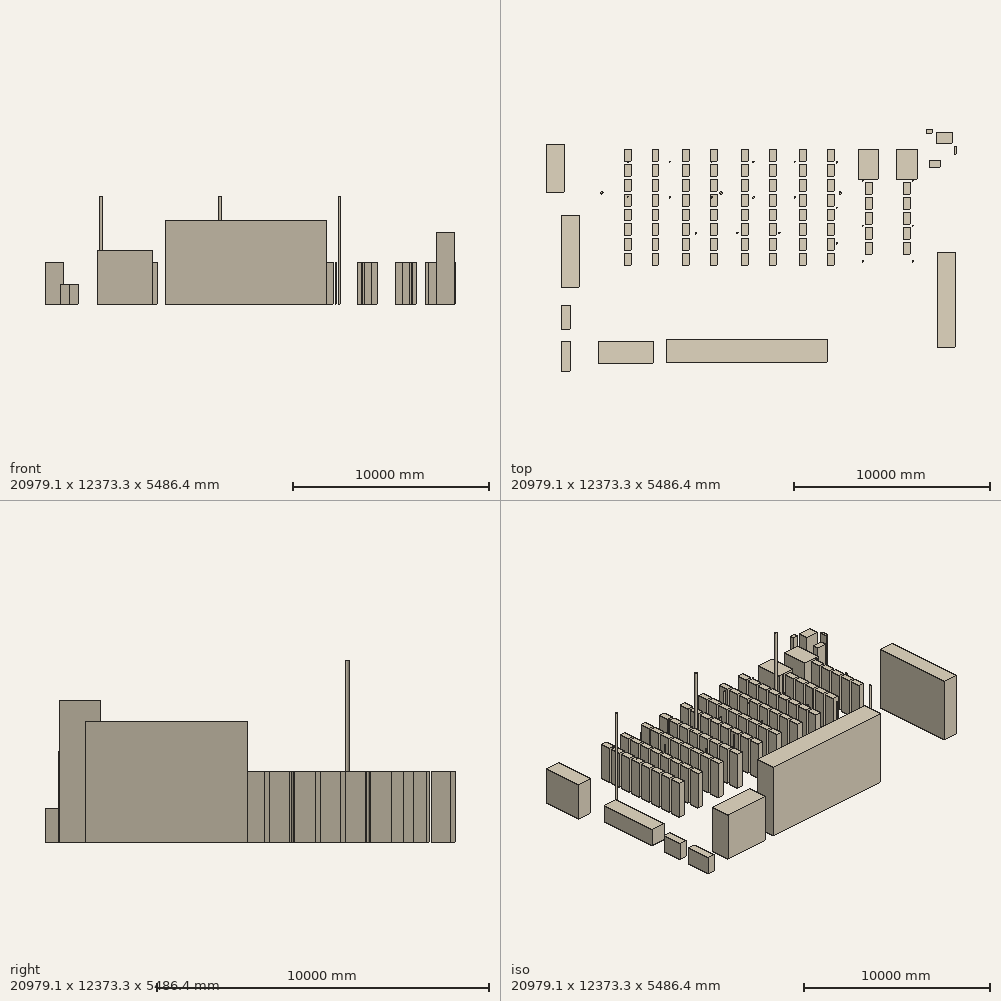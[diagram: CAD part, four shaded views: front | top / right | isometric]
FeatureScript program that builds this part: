
annotation { "Feature Type Name" : "Feature", "Feature Type Description" : "" }
export const myFeature = defineFeature(function(context is Context, id is Id, definition is map)
    precondition{}
    {
        {
            var Q0;
            Q0=qCreatedBy(makeId("Top.planeOp"),FACE);
            var sketch = newSketch(context, id + "F0", { "sketchPlane" : qUnion([Q0])});
            skLineSegment(sketch, "E0", {"start": v(-10502.58, 3251.2) * mm, "end": v(10477.82, 3251.2) * mm});
            skLineSegment(sketch, "E1", {"start": v(-10502.58, 3251.2) * mm, "end": v(-10502.58, 0) * mm});
            skLineSegment(sketch, "E2", {"start": v(-10502.58, 0) * mm, "end": v(-9740.58, 0) * mm});
            skLineSegment(sketch, "E3", {"start": v(-9740.58, 0) * mm, "end": v(-9740.58, -10033) * mm});
            skLineSegment(sketch, "E4", {"start": v(-9740.58, -10033) * mm, "end": v(-7810.18, -10033) * mm});
            skLineSegment(sketch, "E5", {"start": v(-7810.18, -10033) * mm, "end": v(-7810.18, -8839.2) * mm});
            skLineSegment(sketch, "E6", {"start": v(10477.82, 3251.2) * mm, "end": v(10477.82, -8051.8) * mm});
            skLineSegment(sketch, "E7", {"start": v(10477.82, -8051.8) * mm, "end": v(6007.42, -8051.8) * mm});
            skLineSegment(sketch, "E8", {"start": v(6007.42, -8051.8) * mm, "end": v(6007.42, -8839.2) * mm});
            skLineSegment(sketch, "E9", {"start": v(6007.42, -8839.2) * mm, "end": v(-7810.18, -8839.2) * mm});
            skSolve(sketch);
        }
        {
            var Q0;
            Q0=makeQuery(id+"F0.imprint","IMPRINT",FACE,{"disambiguationData":[TD([[makeQuery(id+"F0.imprint","IMPRINT",EDGE,{"derivedFrom":sQuery(id+"F0.wireOp",EDGE,"E0")}),-1.0]])]});
            var sketch = newSketch(context, id + "F1", { "sketchPlane" : qUnion([Q0])});
            skCircle(sketch, "E10", {"center": v(-7657.78, 0) * mm, "radius": 63.5 * mm});
            skCircle(sketch, "E11", {"center": v(-1561.78, 0) * mm, "radius": 63.5 * mm});
            skCircle(sketch, "E12", {"center": v(4534.22, 0) * mm, "radius": 63.5 * mm});
            skSolve(sketch);
        }
        {
            var Q0;
            Q0=makeQuery(id+"F0.imprint","IMPRINT",FACE,{"disambiguationData":[TD([[makeQuery(id+"F0.imprint","IMPRINT",EDGE,{"derivedFrom":sQuery(id+"F0.wireOp",EDGE,"E0")}),-1.0]])]});
            var sketch = newSketch(context, id + "F2", { "sketchPlane" : qUnion([Q0])});
            skLineSegment(sketch, "E13.bottom", {"start": v(9436.42, 3098.8) * mm, "end": v(10249.22, 3098.8) * mm});
            skLineSegment(sketch, "E13.top", {"start": v(9436.42, 2540) * mm, "end": v(10249.22, 2540) * mm});
            skLineSegment(sketch, "E13.left", {"start": v(9436.42, 3098.8) * mm, "end": v(9436.42, 2540) * mm});
            skLineSegment(sketch, "E13.right", {"start": v(10249.22, 3098.8) * mm, "end": v(10249.22, 2540) * mm});
            skLineSegment(sketch, "E14.bottom", {"start": v(9072.21, 1676.4) * mm, "end": v(9681.81, 1676.4) * mm});
            skLineSegment(sketch, "E14.top", {"start": v(9072.21, 1320.8) * mm, "end": v(9681.81, 1320.8) * mm});
            skLineSegment(sketch, "E14.left", {"start": v(9072.21, 1676.4) * mm, "end": v(9072.21, 1320.8) * mm});
            skLineSegment(sketch, "E14.right", {"start": v(9681.81, 1676.4) * mm, "end": v(9681.81, 1320.8) * mm});
            skLineSegment(sketch, "E15.bottom", {"start": v(8928.42, 3251.2) * mm, "end": v(9233.22, 3251.2) * mm});
            skLineSegment(sketch, "E15.top", {"start": v(8928.42, 3048) * mm, "end": v(9233.22, 3048) * mm});
            skLineSegment(sketch, "E15.left", {"start": v(8928.42, 3251.2) * mm, "end": v(8928.42, 3048) * mm});
            skLineSegment(sketch, "E15.right", {"start": v(9233.22, 3251.2) * mm, "end": v(9233.22, 3048) * mm});
            skLineSegment(sketch, "E16.bottom", {"start": v(10477.82, 2387.6) * mm, "end": v(10350.82, 2387.6) * mm});
            skLineSegment(sketch, "E16.top", {"start": v(10477.82, 1981.2) * mm, "end": v(10350.82, 1981.2) * mm});
            skLineSegment(sketch, "E16.left", {"start": v(10477.82, 2387.6) * mm, "end": v(10477.82, 1981.2) * mm});
            skLineSegment(sketch, "E16.right", {"start": v(10350.82, 2387.6) * mm, "end": v(10350.82, 1981.2) * mm});
            skSolve(sketch);
        }
        {
            var Q0;
            Q0=makeQuery(id+"F0.imprint","IMPRINT",FACE,{"disambiguationData":[TD([[makeQuery(id+"F0.imprint","IMPRINT",EDGE,{"derivedFrom":sQuery(id+"F0.wireOp",EDGE,"E0")}),-1.0]])]});
            var sketch = newSketch(context, id + "F3", { "sketchPlane" : qUnion([Q0])});
            skLineSegment(sketch, "E17.bottom", {"start": v(-9740.58, -1168.4) * mm, "end": v(-8826.18, -1168.4) * mm});
            skLineSegment(sketch, "E17.top", {"start": v(-9740.58, -2997.2) * mm, "end": v(-8826.18, -2997.2) * mm});
            skLineSegment(sketch, "E17.left", {"start": v(-9740.58, -1168.4) * mm, "end": v(-9740.58, -2997.2) * mm});
            skLineSegment(sketch, "E17.right", {"start": v(-8826.18, -1168.4) * mm, "end": v(-8826.18, -2997.2) * mm});
            skLineSegment(sketch, "E18.bottom", {"start": v(-9740.58, -9122.12) * mm, "end": v(-9283.38, -9122.12) * mm});
            skLineSegment(sketch, "E18.top", {"start": v(-9740.58, -7598.12) * mm, "end": v(-9283.38, -7598.12) * mm});
            skLineSegment(sketch, "E18.left", {"start": v(-9740.58, -9122.12) * mm, "end": v(-9740.58, -7598.12) * mm});
            skLineSegment(sketch, "E18.right", {"start": v(-9283.38, -9122.12) * mm, "end": v(-9283.38, -7598.12) * mm});
            skLineSegment(sketch, "E19.top", {"start": v(-9740.58, -4826) * mm, "end": v(-8826.18, -4826) * mm});
            skLineSegment(sketch, "E19.left", {"start": v(-9740.58, -2997.2) * mm, "end": v(-9740.58, -4826) * mm});
            skLineSegment(sketch, "E19.right", {"start": v(-8826.18, -2997.2) * mm, "end": v(-8826.18, -4826) * mm});
            skLineSegment(sketch, "E20.bottom", {"start": v(-9740.58, -5740.4) * mm, "end": v(-9283.38, -5740.4) * mm});
            skLineSegment(sketch, "E20.top", {"start": v(-9740.58, -6959.6) * mm, "end": v(-9283.38, -6959.6) * mm});
            skLineSegment(sketch, "E20.left", {"start": v(-9740.58, -5740.4) * mm, "end": v(-9740.58, -6959.6) * mm});
            skLineSegment(sketch, "E20.right", {"start": v(-9283.38, -5740.4) * mm, "end": v(-9283.38, -6959.6) * mm});
            skSolve(sketch);
        }
        {
            var Q0;
            Q0=makeQuery(id+"F0.imprint","IMPRINT",FACE,{"disambiguationData":[TD([[makeQuery(id+"F0.imprint","IMPRINT",EDGE,{"derivedFrom":sQuery(id+"F0.wireOp",EDGE,"E0")}),-1.0]])]});
            var sketch = newSketch(context, id + "F4", { "sketchPlane" : qUnion([Q0])});
            skLineSegment(sketch, "E21.bottom", {"start": v(-7846.94, -8737.6) * mm, "end": v(-6424.54, -8737.6) * mm});
            skLineSegment(sketch, "E21.top", {"start": v(-7846.94, -7569.2) * mm, "end": v(-6424.54, -7569.2) * mm});
            skLineSegment(sketch, "E21.left", {"start": v(-7846.94, -8737.6) * mm, "end": v(-7846.94, -7569.2) * mm});
            skLineSegment(sketch, "E21.right", {"start": v(-6424.54, -8737.6) * mm, "end": v(-6424.54, -7569.2) * mm});
            skLineSegment(sketch, "E22.bottom", {"start": v(-6424.54, -8737.6) * mm, "end": v(-5002.14, -8737.6) * mm});
            skLineSegment(sketch, "E22.top", {"start": v(-6424.54, -7569.2) * mm, "end": v(-5002.14, -7569.2) * mm});
            skLineSegment(sketch, "E22.right", {"start": v(-5002.14, -8737.6) * mm, "end": v(-5002.14, -7569.2) * mm});
            skSolve(sketch);
        }
        {
            var Q0;
            Q0=makeQuery(id+"F0.imprint","IMPRINT",FACE,{"disambiguationData":[TD([[makeQuery(id+"F0.imprint","IMPRINT",EDGE,{"derivedFrom":sQuery(id+"F0.wireOp",EDGE,"E0")}),-1.0]])]});
            var sketch = newSketch(context, id + "F5", { "sketchPlane" : qUnion([Q0])});
            skLineSegment(sketch, "E23.bottom", {"start": v(-4355.78, -8686.8) * mm, "end": v(3873.82, -8686.8) * mm});
            skLineSegment(sketch, "E23.top", {"start": v(-4355.78, -7467.6) * mm, "end": v(3873.82, -7467.6) * mm});
            skLineSegment(sketch, "E23.left", {"start": v(-4355.78, -8686.8) * mm, "end": v(-4355.78, -7467.6) * mm});
            skLineSegment(sketch, "E23.right", {"start": v(3873.82, -8686.8) * mm, "end": v(3873.82, -7467.6) * mm});
            skSolve(sketch);
        }
        {
            var Q0;
            Q0=makeQuery(id+"F0.imprint","IMPRINT",FACE,{"disambiguationData":[TD([[makeQuery(id+"F0.imprint","IMPRINT",EDGE,{"derivedFrom":sQuery(id+"F0.wireOp",EDGE,"E0")}),-1.0]])]});
            var sketch = newSketch(context, id + "F6", { "sketchPlane" : qUnion([Q0])});
            skLineSegment(sketch, "E24.bottom", {"start": v(10427.02, -3022.6) * mm, "end": v(9512.62, -3022.6) * mm});
            skLineSegment(sketch, "E24.top", {"start": v(10427.02, -7899.4) * mm, "end": v(9512.62, -7899.4) * mm});
            skLineSegment(sketch, "E24.left", {"start": v(10427.02, -3022.6) * mm, "end": v(10427.02, -7899.4) * mm});
            skLineSegment(sketch, "E24.right", {"start": v(9512.62, -3022.6) * mm, "end": v(9512.62, -7899.4) * mm});
            skSolve(sketch);
        }
        {
            var Q0;
            Q0=makeQuery(id+"F0.imprint","IMPRINT",FACE,{"disambiguationData":[TD([[makeQuery(id+"F0.imprint","IMPRINT",EDGE,{"derivedFrom":sQuery(id+"F0.wireOp",EDGE,"E0")}),-1.0]])]});
            var sketch = newSketch(context, id + "F7", { "sketchPlane" : qUnion([Q0])});
            skLineSegment(sketch, "E25.bottom", {"start": v(8462.61, 1719.58) * mm, "end": v(7421.21, 1719.58) * mm});
            skLineSegment(sketch, "E25.top", {"start": v(8462.61, 2235.2) * mm, "end": v(7421.21, 2235.2) * mm});
            skLineSegment(sketch, "E25.left", {"start": v(8462.61, 1719.58) * mm, "end": v(8462.61, 2235.2) * mm});
            skLineSegment(sketch, "E25.right", {"start": v(7421.21, 1719.58) * mm, "end": v(7421.21, 2235.2) * mm});
            skPoint(sketch, "E25.middle", {"position": v(7941.91, 1977.4) * mm});
            skLineSegment(sketch, "E26.bottom", {"start": v(6506.81, 1719.58) * mm, "end": v(5465.41, 1719.58) * mm});
            skLineSegment(sketch, "E26.top", {"start": v(6506.81, 2235.2) * mm, "end": v(5465.41, 2235.2) * mm});
            skLineSegment(sketch, "E26.left", {"start": v(6506.81, 1719.58) * mm, "end": v(6506.81, 2235.2) * mm});
            skLineSegment(sketch, "E26.right", {"start": v(5465.41, 1719.58) * mm, "end": v(5465.41, 2235.2) * mm});
            skPoint(sketch, "E26.middle", {"position": v(5986.11, 1977.4) * mm});
            skLineSegment(sketch, "E27.bottom", {"start": v(8462.61, 1203.96) * mm, "end": v(7421.21, 1203.96) * mm});
            skLineSegment(sketch, "E27.left", {"start": v(8462.61, 1203.96) * mm, "end": v(8462.61, 1719.58) * mm});
            skLineSegment(sketch, "E27.right", {"start": v(7421.21, 1203.96) * mm, "end": v(7421.21, 1719.58) * mm});
            skPoint(sketch, "E27.middle", {"position": v(7941.91, 1461.77) * mm});
            skLineSegment(sketch, "E28.bottom", {"start": v(6506.81, 1203.96) * mm, "end": v(5465.41, 1203.96) * mm});
            skLineSegment(sketch, "E28.left", {"start": v(6506.81, 1203.96) * mm, "end": v(6506.81, 1719.58) * mm});
            skLineSegment(sketch, "E28.right", {"start": v(5465.41, 1203.96) * mm, "end": v(5465.41, 1719.58) * mm});
            skPoint(sketch, "E28.middle", {"position": v(5986.11, 1461.77) * mm});
            skLineSegment(sketch, "E29.bottom", {"start": v(6506.81, 688.34) * mm, "end": v(5465.41, 688.34) * mm});
            skLineSegment(sketch, "E29.left", {"start": v(6506.81, 688.34) * mm, "end": v(6506.81, 1203.96) * mm});
            skLineSegment(sketch, "E29.right", {"start": v(5465.41, 688.34) * mm, "end": v(5465.41, 1203.96) * mm});
            skPoint(sketch, "E29.middle", {"position": v(5986.11, 946.15) * mm});
            skLineSegment(sketch, "E30.bottom", {"start": v(8462.61, 688.34) * mm, "end": v(7421.21, 688.34) * mm});
            skLineSegment(sketch, "E30.left", {"start": v(8462.61, 688.34) * mm, "end": v(8462.61, 1203.96) * mm});
            skLineSegment(sketch, "E30.right", {"start": v(7421.21, 688.34) * mm, "end": v(7421.21, 1203.96) * mm});
            skPoint(sketch, "E30.middle", {"position": v(7941.91, 946.15) * mm});
            skLineSegment(sketch, "E31.bottom", {"start": v(6163.91, -73.66) * mm, "end": v(5808.31, -73.66) * mm});
            skLineSegment(sketch, "E31.top", {"start": v(6163.91, 535.94) * mm, "end": v(5808.31, 535.94) * mm});
            skLineSegment(sketch, "E31.left", {"start": v(6163.91, -73.66) * mm, "end": v(6163.91, 535.94) * mm});
            skLineSegment(sketch, "E31.right", {"start": v(5808.31, -73.66) * mm, "end": v(5808.31, 535.94) * mm});
            skPoint(sketch, "E31.middle", {"position": v(5986.11, 231.14) * mm});
            skLineSegment(sketch, "E32.bottom", {"start": v(6163.91, -835.66) * mm, "end": v(5808.31, -835.66) * mm});
            skLineSegment(sketch, "E32.top", {"start": v(6163.91, -226.06) * mm, "end": v(5808.31, -226.06) * mm});
            skLineSegment(sketch, "E32.left", {"start": v(6163.91, -835.66) * mm, "end": v(6163.91, -226.06) * mm});
            skLineSegment(sketch, "E32.right", {"start": v(5808.31, -835.66) * mm, "end": v(5808.31, -226.06) * mm});
            skPoint(sketch, "E32.middle", {"position": v(5986.11, -530.86) * mm});
            skLineSegment(sketch, "E33.bottom", {"start": v(6163.91, -1597.66) * mm, "end": v(5808.31, -1597.66) * mm});
            skLineSegment(sketch, "E33.top", {"start": v(6163.91, -988.06) * mm, "end": v(5808.31, -988.06) * mm});
            skLineSegment(sketch, "E33.left", {"start": v(6163.91, -1597.66) * mm, "end": v(6163.91, -988.06) * mm});
            skLineSegment(sketch, "E33.right", {"start": v(5808.31, -1597.66) * mm, "end": v(5808.31, -988.06) * mm});
            skPoint(sketch, "E33.middle", {"position": v(5986.11, -1292.86) * mm});
            skLineSegment(sketch, "E34.bottom", {"start": v(7764.11, -73.66) * mm, "end": v(8119.71, -73.66) * mm});
            skLineSegment(sketch, "E34.top", {"start": v(7764.11, 535.94) * mm, "end": v(8119.71, 535.94) * mm});
            skLineSegment(sketch, "E34.left", {"start": v(7764.11, -73.66) * mm, "end": v(7764.11, 535.94) * mm});
            skLineSegment(sketch, "E34.right", {"start": v(8119.71, -73.66) * mm, "end": v(8119.71, 535.94) * mm});
            skPoint(sketch, "E34.middle", {"position": v(7941.91, 231.14) * mm});
            skLineSegment(sketch, "E35.bottom", {"start": v(7764.11, -835.66) * mm, "end": v(8119.71, -835.66) * mm});
            skLineSegment(sketch, "E35.top", {"start": v(7764.11, -226.06) * mm, "end": v(8119.71, -226.06) * mm});
            skLineSegment(sketch, "E35.left", {"start": v(7764.11, -835.66) * mm, "end": v(7764.11, -226.06) * mm});
            skLineSegment(sketch, "E35.right", {"start": v(8119.71, -835.66) * mm, "end": v(8119.71, -226.06) * mm});
            skPoint(sketch, "E35.middle", {"position": v(7941.91, -530.86) * mm});
            skLineSegment(sketch, "E36.bottom", {"start": v(7764.11, -1597.66) * mm, "end": v(8119.71, -1597.66) * mm});
            skLineSegment(sketch, "E36.top", {"start": v(7764.11, -988.06) * mm, "end": v(8119.71, -988.06) * mm});
            skLineSegment(sketch, "E36.left", {"start": v(7764.11, -1597.66) * mm, "end": v(7764.11, -988.06) * mm});
            skLineSegment(sketch, "E36.right", {"start": v(8119.71, -1597.66) * mm, "end": v(8119.71, -988.06) * mm});
            skPoint(sketch, "E36.middle", {"position": v(7941.91, -1292.86) * mm});
            skLineSegment(sketch, "E37.bottom", {"start": v(5808.31, -1750.06) * mm, "end": v(6163.91, -1750.06) * mm});
            skLineSegment(sketch, "E37.top", {"start": v(5808.31, -2359.66) * mm, "end": v(6163.91, -2359.66) * mm});
            skLineSegment(sketch, "E37.left", {"start": v(5808.31, -1750.06) * mm, "end": v(5808.31, -2359.66) * mm});
            skLineSegment(sketch, "E37.right", {"start": v(6163.91, -1750.06) * mm, "end": v(6163.91, -2359.66) * mm});
            skPoint(sketch, "E37.middle", {"position": v(5986.11, -2054.86) * mm});
            skLineSegment(sketch, "E38.bottom", {"start": v(7764.11, -1750.06) * mm, "end": v(8119.71, -1750.06) * mm});
            skLineSegment(sketch, "E38.top", {"start": v(7764.11, -2359.66) * mm, "end": v(8119.71, -2359.66) * mm});
            skLineSegment(sketch, "E38.left", {"start": v(7764.11, -1750.06) * mm, "end": v(7764.11, -2359.66) * mm});
            skLineSegment(sketch, "E38.right", {"start": v(8119.71, -1750.06) * mm, "end": v(8119.71, -2359.66) * mm});
            skPoint(sketch, "E38.middle", {"position": v(7941.91, -2054.86) * mm});
            skLineSegment(sketch, "E39.bottom", {"start": v(5808.31, -2512.06) * mm, "end": v(6163.91, -2512.06) * mm});
            skLineSegment(sketch, "E39.top", {"start": v(5808.31, -3121.66) * mm, "end": v(6163.91, -3121.66) * mm});
            skLineSegment(sketch, "E39.left", {"start": v(5808.31, -2512.06) * mm, "end": v(5808.31, -3121.66) * mm});
            skLineSegment(sketch, "E39.right", {"start": v(6163.91, -2512.06) * mm, "end": v(6163.91, -3121.66) * mm});
            skPoint(sketch, "E39.middle", {"position": v(5986.11, -2816.86) * mm});
            skLineSegment(sketch, "E40.bottom", {"start": v(7764.11, -2512.06) * mm, "end": v(8119.71, -2512.06) * mm});
            skLineSegment(sketch, "E40.top", {"start": v(7764.11, -3121.66) * mm, "end": v(8119.71, -3121.66) * mm});
            skLineSegment(sketch, "E40.left", {"start": v(7764.11, -2512.06) * mm, "end": v(7764.11, -3121.66) * mm});
            skLineSegment(sketch, "E40.right", {"start": v(8119.71, -2512.06) * mm, "end": v(8119.71, -3121.66) * mm});
            skPoint(sketch, "E40.middle", {"position": v(7941.91, -2816.86) * mm});
            skSolve(sketch);
        }
        {
            var Q0;
            Q0=makeQuery(id+"F0.imprint","IMPRINT",FACE,{"disambiguationData":[TD([[makeQuery(id+"F0.imprint","IMPRINT",EDGE,{"derivedFrom":sQuery(id+"F0.wireOp",EDGE,"E0")}),-1.0]])]});
            var sketch = newSketch(context, id + "F8", { "sketchPlane" : qUnion([Q0])});
            skLineSegment(sketch, "E41.bottom", {"start": v(3890.61, 2235.2) * mm, "end": v(4246.21, 2235.2) * mm});
            skLineSegment(sketch, "E41.top", {"start": v(3890.61, 1625.6) * mm, "end": v(4246.21, 1625.6) * mm});
            skLineSegment(sketch, "E41.left", {"start": v(3890.61, 2235.2) * mm, "end": v(3890.61, 1625.6) * mm});
            skLineSegment(sketch, "E41.right", {"start": v(4246.21, 2235.2) * mm, "end": v(4246.21, 1625.6) * mm});
            skPoint(sketch, "E41.middle", {"position": v(4068.41, 1930.4) * mm});
            skLineSegment(sketch, "E42.bottom", {"start": v(3890.61, 1473.2) * mm, "end": v(4246.21, 1473.2) * mm});
            skLineSegment(sketch, "E42.top", {"start": v(3890.61, 863.6) * mm, "end": v(4246.21, 863.6) * mm});
            skLineSegment(sketch, "E42.left", {"start": v(3890.61, 1473.2) * mm, "end": v(3890.61, 863.6) * mm});
            skLineSegment(sketch, "E42.right", {"start": v(4246.21, 1473.2) * mm, "end": v(4246.21, 863.6) * mm});
            skPoint(sketch, "E42.middle", {"position": v(4068.41, 1168.4) * mm});
            skLineSegment(sketch, "E43.bottom", {"start": v(2468.21, 2235.2) * mm, "end": v(2823.81, 2235.2) * mm});
            skLineSegment(sketch, "E43.top", {"start": v(2468.21, 1625.6) * mm, "end": v(2823.81, 1625.6) * mm});
            skLineSegment(sketch, "E43.left", {"start": v(2468.21, 2235.2) * mm, "end": v(2468.21, 1625.6) * mm});
            skLineSegment(sketch, "E43.right", {"start": v(2823.81, 2235.2) * mm, "end": v(2823.81, 1625.6) * mm});
            skPoint(sketch, "E43.middle", {"position": v(2646.01, 1930.4) * mm});
            skLineSegment(sketch, "E44.bottom", {"start": v(2468.21, 1473.2) * mm, "end": v(2823.81, 1473.2) * mm});
            skLineSegment(sketch, "E44.top", {"start": v(2468.21, 863.6) * mm, "end": v(2823.81, 863.6) * mm});
            skLineSegment(sketch, "E44.left", {"start": v(2468.21, 1473.2) * mm, "end": v(2468.21, 863.6) * mm});
            skLineSegment(sketch, "E44.right", {"start": v(2823.81, 1473.2) * mm, "end": v(2823.81, 863.6) * mm});
            skPoint(sketch, "E44.middle", {"position": v(2646.01, 1168.4) * mm});
            skLineSegment(sketch, "E45.bottom", {"start": v(2468.21, 711.2) * mm, "end": v(2823.81, 711.2) * mm});
            skLineSegment(sketch, "E45.top", {"start": v(2468.21, 101.6) * mm, "end": v(2823.81, 101.6) * mm});
            skLineSegment(sketch, "E45.left", {"start": v(2468.21, 711.2) * mm, "end": v(2468.21, 101.6) * mm});
            skLineSegment(sketch, "E45.right", {"start": v(2823.81, 711.2) * mm, "end": v(2823.81, 101.6) * mm});
            skPoint(sketch, "E45.middle", {"position": v(2646.01, 406.4) * mm});
            skLineSegment(sketch, "E46.bottom", {"start": v(3890.61, 711.2) * mm, "end": v(4246.21, 711.2) * mm});
            skLineSegment(sketch, "E46.top", {"start": v(3890.61, 101.6) * mm, "end": v(4246.21, 101.6) * mm});
            skLineSegment(sketch, "E46.left", {"start": v(3890.61, 711.2) * mm, "end": v(3890.61, 101.6) * mm});
            skLineSegment(sketch, "E46.right", {"start": v(4246.21, 711.2) * mm, "end": v(4246.21, 101.6) * mm});
            skPoint(sketch, "E46.middle", {"position": v(4068.41, 406.4) * mm});
            skLineSegment(sketch, "E47.bottom", {"start": v(2468.21, -50.8) * mm, "end": v(2823.81, -50.8) * mm});
            skLineSegment(sketch, "E47.top", {"start": v(2468.21, -660.4) * mm, "end": v(2823.81, -660.4) * mm});
            skLineSegment(sketch, "E47.left", {"start": v(2468.21, -50.8) * mm, "end": v(2468.21, -660.4) * mm});
            skLineSegment(sketch, "E47.right", {"start": v(2823.81, -50.8) * mm, "end": v(2823.81, -660.4) * mm});
            skPoint(sketch, "E47.middle", {"position": v(2646.01, -355.6) * mm});
            skLineSegment(sketch, "E48.bottom", {"start": v(3890.61, -50.8) * mm, "end": v(4246.21, -50.8) * mm});
            skLineSegment(sketch, "E48.top", {"start": v(3890.61, -660.4) * mm, "end": v(4246.21, -660.4) * mm});
            skLineSegment(sketch, "E48.left", {"start": v(3890.61, -50.8) * mm, "end": v(3890.61, -660.4) * mm});
            skLineSegment(sketch, "E48.right", {"start": v(4246.21, -50.8) * mm, "end": v(4246.21, -660.4) * mm});
            skPoint(sketch, "E48.middle", {"position": v(4068.41, -355.6) * mm});
            skLineSegment(sketch, "E49.bottom", {"start": v(2468.21, -812.8) * mm, "end": v(2823.81, -812.8) * mm});
            skLineSegment(sketch, "E49.top", {"start": v(2468.21, -1422.4) * mm, "end": v(2823.81, -1422.4) * mm});
            skLineSegment(sketch, "E49.left", {"start": v(2468.21, -812.8) * mm, "end": v(2468.21, -1422.4) * mm});
            skLineSegment(sketch, "E49.right", {"start": v(2823.81, -812.8) * mm, "end": v(2823.81, -1422.4) * mm});
            skPoint(sketch, "E49.middle", {"position": v(2646.01, -1117.6) * mm});
            skLineSegment(sketch, "E50.bottom", {"start": v(3890.61, -812.8) * mm, "end": v(4246.21, -812.8) * mm});
            skLineSegment(sketch, "E50.top", {"start": v(3890.61, -1422.4) * mm, "end": v(4246.21, -1422.4) * mm});
            skLineSegment(sketch, "E50.left", {"start": v(3890.61, -812.8) * mm, "end": v(3890.61, -1422.4) * mm});
            skLineSegment(sketch, "E50.right", {"start": v(4246.21, -812.8) * mm, "end": v(4246.21, -1422.4) * mm});
            skPoint(sketch, "E50.middle", {"position": v(4068.41, -1117.6) * mm});
            skLineSegment(sketch, "E51.bottom", {"start": v(2468.21, -1574.8) * mm, "end": v(2823.81, -1574.8) * mm});
            skLineSegment(sketch, "E51.top", {"start": v(2468.21, -2184.4) * mm, "end": v(2823.81, -2184.4) * mm});
            skLineSegment(sketch, "E51.left", {"start": v(2468.21, -1574.8) * mm, "end": v(2468.21, -2184.4) * mm});
            skLineSegment(sketch, "E51.right", {"start": v(2823.81, -1574.8) * mm, "end": v(2823.81, -2184.4) * mm});
            skPoint(sketch, "E51.middle", {"position": v(2646.01, -1879.6) * mm});
            skLineSegment(sketch, "E52.bottom", {"start": v(3890.61, -1574.8) * mm, "end": v(4246.21, -1574.8) * mm});
            skLineSegment(sketch, "E52.top", {"start": v(3890.61, -2184.4) * mm, "end": v(4246.21, -2184.4) * mm});
            skLineSegment(sketch, "E52.left", {"start": v(3890.61, -1574.8) * mm, "end": v(3890.61, -2184.4) * mm});
            skLineSegment(sketch, "E52.right", {"start": v(4246.21, -1574.8) * mm, "end": v(4246.21, -2184.4) * mm});
            skPoint(sketch, "E52.middle", {"position": v(4068.41, -1879.6) * mm});
            skLineSegment(sketch, "E53.bottom", {"start": v(2468.21, -2336.8) * mm, "end": v(2823.81, -2336.8) * mm});
            skLineSegment(sketch, "E53.top", {"start": v(2468.21, -2946.4) * mm, "end": v(2823.81, -2946.4) * mm});
            skLineSegment(sketch, "E53.left", {"start": v(2468.21, -2336.8) * mm, "end": v(2468.21, -2946.4) * mm});
            skLineSegment(sketch, "E53.right", {"start": v(2823.81, -2336.8) * mm, "end": v(2823.81, -2946.4) * mm});
            skPoint(sketch, "E53.middle", {"position": v(2646.01, -2641.6) * mm});
            skLineSegment(sketch, "E54.bottom", {"start": v(3890.61, -2336.8) * mm, "end": v(4246.21, -2336.8) * mm});
            skLineSegment(sketch, "E54.top", {"start": v(3890.61, -2946.4) * mm, "end": v(4246.21, -2946.4) * mm});
            skLineSegment(sketch, "E54.left", {"start": v(3890.61, -2336.8) * mm, "end": v(3890.61, -2946.4) * mm});
            skLineSegment(sketch, "E54.right", {"start": v(4246.21, -2336.8) * mm, "end": v(4246.21, -2946.4) * mm});
            skPoint(sketch, "E54.middle", {"position": v(4068.41, -2641.6) * mm});
            skLineSegment(sketch, "E55.bottom", {"start": v(2468.21, -3098.8) * mm, "end": v(2823.81, -3098.8) * mm});
            skLineSegment(sketch, "E55.top", {"start": v(2468.21, -3708.4) * mm, "end": v(2823.81, -3708.4) * mm});
            skLineSegment(sketch, "E55.left", {"start": v(2468.21, -3098.8) * mm, "end": v(2468.21, -3708.4) * mm});
            skLineSegment(sketch, "E55.right", {"start": v(2823.81, -3098.8) * mm, "end": v(2823.81, -3708.4) * mm});
            skPoint(sketch, "E55.middle", {"position": v(2646.01, -3403.6) * mm});
            skLineSegment(sketch, "E56.bottom", {"start": v(4246.21, -3098.8) * mm, "end": v(3890.61, -3098.8) * mm});
            skLineSegment(sketch, "E56.top", {"start": v(4246.21, -3708.4) * mm, "end": v(3890.61, -3708.4) * mm});
            skLineSegment(sketch, "E56.left", {"start": v(4246.21, -3098.8) * mm, "end": v(4246.21, -3708.4) * mm});
            skLineSegment(sketch, "E56.right", {"start": v(3890.61, -3098.8) * mm, "end": v(3890.61, -3708.4) * mm});
            skPoint(sketch, "E56.middle", {"position": v(4068.41, -3403.6) * mm});
            skSolve(sketch);
        }
        {
            var Q0;
            Q0=makeQuery(id+"F0.imprint","IMPRINT",FACE,{"disambiguationData":[TD([[makeQuery(id+"F0.imprint","IMPRINT",EDGE,{"derivedFrom":sQuery(id+"F0.wireOp",EDGE,"E0")}),-1.0]])]});
            var sketch = newSketch(context, id + "F9", { "sketchPlane" : qUnion([Q0])});
            skLineSegment(sketch, "E57.bottom", {"start": v(893.41, 2235.2) * mm, "end": v(1249.01, 2235.2) * mm});
            skLineSegment(sketch, "E57.top", {"start": v(893.41, 1625.6) * mm, "end": v(1249.01, 1625.6) * mm});
            skLineSegment(sketch, "E57.left", {"start": v(893.41, 2235.2) * mm, "end": v(893.41, 1625.6) * mm});
            skLineSegment(sketch, "E57.right", {"start": v(1249.01, 2235.2) * mm, "end": v(1249.01, 1625.6) * mm});
            skPoint(sketch, "E57.middle", {"position": v(1071.21, 1930.4) * mm});
            skLineSegment(sketch, "E58.bottom", {"start": v(893.41, 1473.2) * mm, "end": v(1249.01, 1473.2) * mm});
            skLineSegment(sketch, "E58.top", {"start": v(893.41, 863.6) * mm, "end": v(1249.01, 863.6) * mm});
            skLineSegment(sketch, "E58.left", {"start": v(893.41, 1473.2) * mm, "end": v(893.41, 863.6) * mm});
            skLineSegment(sketch, "E58.right", {"start": v(1249.01, 1473.2) * mm, "end": v(1249.01, 863.6) * mm});
            skPoint(sketch, "E58.middle", {"position": v(1071.21, 1168.4) * mm});
            skLineSegment(sketch, "E59.bottom", {"start": v(-528.99, 2235.2) * mm, "end": v(-173.39, 2235.2) * mm});
            skLineSegment(sketch, "E59.top", {"start": v(-528.99, 1625.6) * mm, "end": v(-173.39, 1625.6) * mm});
            skLineSegment(sketch, "E59.left", {"start": v(-528.99, 2235.2) * mm, "end": v(-528.99, 1625.6) * mm});
            skLineSegment(sketch, "E59.right", {"start": v(-173.39, 2235.2) * mm, "end": v(-173.39, 1625.6) * mm});
            skPoint(sketch, "E59.middle", {"position": v(-351.19, 1930.4) * mm});
            skLineSegment(sketch, "E60.bottom", {"start": v(-528.99, 1473.2) * mm, "end": v(-173.39, 1473.2) * mm});
            skLineSegment(sketch, "E60.top", {"start": v(-528.99, 863.6) * mm, "end": v(-173.39, 863.6) * mm});
            skLineSegment(sketch, "E60.left", {"start": v(-528.99, 1473.2) * mm, "end": v(-528.99, 863.6) * mm});
            skLineSegment(sketch, "E60.right", {"start": v(-173.39, 1473.2) * mm, "end": v(-173.39, 863.6) * mm});
            skPoint(sketch, "E60.middle", {"position": v(-351.19, 1168.4) * mm});
            skLineSegment(sketch, "E61.bottom", {"start": v(-528.99, 711.2) * mm, "end": v(-173.39, 711.2) * mm});
            skLineSegment(sketch, "E61.top", {"start": v(-528.99, 101.6) * mm, "end": v(-173.39, 101.6) * mm});
            skLineSegment(sketch, "E61.left", {"start": v(-528.99, 711.2) * mm, "end": v(-528.99, 101.6) * mm});
            skLineSegment(sketch, "E61.right", {"start": v(-173.39, 711.2) * mm, "end": v(-173.39, 101.6) * mm});
            skPoint(sketch, "E61.middle", {"position": v(-351.19, 406.4) * mm});
            skLineSegment(sketch, "E62.bottom", {"start": v(893.41, 711.2) * mm, "end": v(1249.01, 711.2) * mm});
            skLineSegment(sketch, "E62.top", {"start": v(893.41, 101.6) * mm, "end": v(1249.01, 101.6) * mm});
            skLineSegment(sketch, "E62.left", {"start": v(893.41, 711.2) * mm, "end": v(893.41, 101.6) * mm});
            skLineSegment(sketch, "E62.right", {"start": v(1249.01, 711.2) * mm, "end": v(1249.01, 101.6) * mm});
            skPoint(sketch, "E62.middle", {"position": v(1071.21, 406.4) * mm});
            skLineSegment(sketch, "E63.bottom", {"start": v(-528.99, -50.8) * mm, "end": v(-173.39, -50.8) * mm});
            skLineSegment(sketch, "E63.top", {"start": v(-528.99, -660.4) * mm, "end": v(-173.39, -660.4) * mm});
            skLineSegment(sketch, "E63.left", {"start": v(-528.99, -50.8) * mm, "end": v(-528.99, -660.4) * mm});
            skLineSegment(sketch, "E63.right", {"start": v(-173.39, -50.8) * mm, "end": v(-173.39, -660.4) * mm});
            skPoint(sketch, "E63.middle", {"position": v(-351.19, -355.6) * mm});
            skLineSegment(sketch, "E64.bottom", {"start": v(893.41, -50.8) * mm, "end": v(1249.01, -50.8) * mm});
            skLineSegment(sketch, "E64.top", {"start": v(893.41, -660.4) * mm, "end": v(1249.01, -660.4) * mm});
            skLineSegment(sketch, "E64.left", {"start": v(893.41, -50.8) * mm, "end": v(893.41, -660.4) * mm});
            skLineSegment(sketch, "E64.right", {"start": v(1249.01, -50.8) * mm, "end": v(1249.01, -660.4) * mm});
            skPoint(sketch, "E64.middle", {"position": v(1071.21, -355.6) * mm});
            skLineSegment(sketch, "E65.bottom", {"start": v(-528.99, -812.8) * mm, "end": v(-173.39, -812.8) * mm});
            skLineSegment(sketch, "E65.top", {"start": v(-528.99, -1422.4) * mm, "end": v(-173.39, -1422.4) * mm});
            skLineSegment(sketch, "E65.left", {"start": v(-528.99, -812.8) * mm, "end": v(-528.99, -1422.4) * mm});
            skLineSegment(sketch, "E65.right", {"start": v(-173.39, -812.8) * mm, "end": v(-173.39, -1422.4) * mm});
            skPoint(sketch, "E65.middle", {"position": v(-351.19, -1117.6) * mm});
            skLineSegment(sketch, "E66.bottom", {"start": v(893.41, -812.8) * mm, "end": v(1249.01, -812.8) * mm});
            skLineSegment(sketch, "E66.top", {"start": v(893.41, -1422.4) * mm, "end": v(1249.01, -1422.4) * mm});
            skLineSegment(sketch, "E66.left", {"start": v(893.41, -812.8) * mm, "end": v(893.41, -1422.4) * mm});
            skLineSegment(sketch, "E66.right", {"start": v(1249.01, -812.8) * mm, "end": v(1249.01, -1422.4) * mm});
            skPoint(sketch, "E66.middle", {"position": v(1071.21, -1117.6) * mm});
            skLineSegment(sketch, "E67.bottom", {"start": v(-528.99, -1574.8) * mm, "end": v(-173.39, -1574.8) * mm});
            skLineSegment(sketch, "E67.top", {"start": v(-528.99, -2184.4) * mm, "end": v(-173.39, -2184.4) * mm});
            skLineSegment(sketch, "E67.left", {"start": v(-528.99, -1574.8) * mm, "end": v(-528.99, -2184.4) * mm});
            skLineSegment(sketch, "E67.right", {"start": v(-173.39, -1574.8) * mm, "end": v(-173.39, -2184.4) * mm});
            skPoint(sketch, "E67.middle", {"position": v(-351.19, -1879.6) * mm});
            skLineSegment(sketch, "E68.bottom", {"start": v(893.41, -1574.8) * mm, "end": v(1249.01, -1574.8) * mm});
            skLineSegment(sketch, "E68.top", {"start": v(893.41, -2184.4) * mm, "end": v(1249.01, -2184.4) * mm});
            skLineSegment(sketch, "E68.left", {"start": v(893.41, -1574.8) * mm, "end": v(893.41, -2184.4) * mm});
            skLineSegment(sketch, "E68.right", {"start": v(1249.01, -1574.8) * mm, "end": v(1249.01, -2184.4) * mm});
            skPoint(sketch, "E68.middle", {"position": v(1071.21, -1879.6) * mm});
            skLineSegment(sketch, "E69.bottom", {"start": v(-528.99, -2336.8) * mm, "end": v(-173.39, -2336.8) * mm});
            skLineSegment(sketch, "E69.top", {"start": v(-528.99, -2946.4) * mm, "end": v(-173.39, -2946.4) * mm});
            skLineSegment(sketch, "E69.left", {"start": v(-528.99, -2336.8) * mm, "end": v(-528.99, -2946.4) * mm});
            skLineSegment(sketch, "E69.right", {"start": v(-173.39, -2336.8) * mm, "end": v(-173.39, -2946.4) * mm});
            skPoint(sketch, "E69.middle", {"position": v(-351.19, -2641.6) * mm});
            skLineSegment(sketch, "E70.bottom", {"start": v(893.41, -2336.8) * mm, "end": v(1249.01, -2336.8) * mm});
            skLineSegment(sketch, "E70.top", {"start": v(893.41, -2946.4) * mm, "end": v(1249.01, -2946.4) * mm});
            skLineSegment(sketch, "E70.left", {"start": v(893.41, -2336.8) * mm, "end": v(893.41, -2946.4) * mm});
            skLineSegment(sketch, "E70.right", {"start": v(1249.01, -2336.8) * mm, "end": v(1249.01, -2946.4) * mm});
            skPoint(sketch, "E70.middle", {"position": v(1071.21, -2641.6) * mm});
            skLineSegment(sketch, "E71.bottom", {"start": v(-528.99, -3098.8) * mm, "end": v(-173.39, -3098.8) * mm});
            skLineSegment(sketch, "E71.top", {"start": v(-528.99, -3708.4) * mm, "end": v(-173.39, -3708.4) * mm});
            skLineSegment(sketch, "E71.left", {"start": v(-528.99, -3098.8) * mm, "end": v(-528.99, -3708.4) * mm});
            skLineSegment(sketch, "E71.right", {"start": v(-173.39, -3098.8) * mm, "end": v(-173.39, -3708.4) * mm});
            skPoint(sketch, "E71.middle", {"position": v(-351.19, -3403.6) * mm});
            skLineSegment(sketch, "E72.bottom", {"start": v(1249.01, -3098.8) * mm, "end": v(893.41, -3098.8) * mm});
            skLineSegment(sketch, "E72.top", {"start": v(1249.01, -3708.4) * mm, "end": v(893.41, -3708.4) * mm});
            skLineSegment(sketch, "E72.left", {"start": v(1249.01, -3098.8) * mm, "end": v(1249.01, -3708.4) * mm});
            skLineSegment(sketch, "E72.right", {"start": v(893.41, -3098.8) * mm, "end": v(893.41, -3708.4) * mm});
            skPoint(sketch, "E72.middle", {"position": v(1071.21, -3403.6) * mm});
            skSolve(sketch);
        }
        {
            var Q0;
            Q0=makeQuery(id+"F0.imprint","IMPRINT",FACE,{"disambiguationData":[TD([[makeQuery(id+"F0.imprint","IMPRINT",EDGE,{"derivedFrom":sQuery(id+"F0.wireOp",EDGE,"E0")}),-1.0]])]});
            var sketch = newSketch(context, id + "F10", { "sketchPlane" : qUnion([Q0])});
            skLineSegment(sketch, "E73.bottom", {"start": v(-2103.79, 2235.2) * mm, "end": v(-1748.19, 2235.2) * mm});
            skLineSegment(sketch, "E73.top", {"start": v(-2103.79, 1625.6) * mm, "end": v(-1748.19, 1625.6) * mm});
            skLineSegment(sketch, "E73.left", {"start": v(-2103.79, 2235.2) * mm, "end": v(-2103.79, 1625.6) * mm});
            skLineSegment(sketch, "E73.right", {"start": v(-1748.19, 2235.2) * mm, "end": v(-1748.19, 1625.6) * mm});
            skPoint(sketch, "E73.middle", {"position": v(-1925.99, 1930.4) * mm});
            skLineSegment(sketch, "E74.bottom", {"start": v(-2103.79, 1473.2) * mm, "end": v(-1748.19, 1473.2) * mm});
            skLineSegment(sketch, "E74.top", {"start": v(-2103.79, 863.6) * mm, "end": v(-1748.19, 863.6) * mm});
            skLineSegment(sketch, "E74.left", {"start": v(-2103.79, 1473.2) * mm, "end": v(-2103.79, 863.6) * mm});
            skLineSegment(sketch, "E74.right", {"start": v(-1748.19, 1473.2) * mm, "end": v(-1748.19, 863.6) * mm});
            skPoint(sketch, "E74.middle", {"position": v(-1925.99, 1168.4) * mm});
            skLineSegment(sketch, "E75.bottom", {"start": v(-3526.19, 2235.2) * mm, "end": v(-3170.59, 2235.2) * mm});
            skLineSegment(sketch, "E75.top", {"start": v(-3526.19, 1625.6) * mm, "end": v(-3170.59, 1625.6) * mm});
            skLineSegment(sketch, "E75.left", {"start": v(-3526.19, 2235.2) * mm, "end": v(-3526.19, 1625.6) * mm});
            skLineSegment(sketch, "E75.right", {"start": v(-3170.59, 2235.2) * mm, "end": v(-3170.59, 1625.6) * mm});
            skPoint(sketch, "E75.middle", {"position": v(-3348.39, 1930.4) * mm});
            skLineSegment(sketch, "E76.bottom", {"start": v(-3526.19, 1473.2) * mm, "end": v(-3170.59, 1473.2) * mm});
            skLineSegment(sketch, "E76.top", {"start": v(-3526.19, 863.6) * mm, "end": v(-3170.59, 863.6) * mm});
            skLineSegment(sketch, "E76.left", {"start": v(-3526.19, 1473.2) * mm, "end": v(-3526.19, 863.6) * mm});
            skLineSegment(sketch, "E76.right", {"start": v(-3170.59, 1473.2) * mm, "end": v(-3170.59, 863.6) * mm});
            skPoint(sketch, "E76.middle", {"position": v(-3348.39, 1168.4) * mm});
            skLineSegment(sketch, "E77.bottom", {"start": v(-3526.19, 711.2) * mm, "end": v(-3170.59, 711.2) * mm});
            skLineSegment(sketch, "E77.top", {"start": v(-3526.19, 101.6) * mm, "end": v(-3170.59, 101.6) * mm});
            skLineSegment(sketch, "E77.left", {"start": v(-3526.19, 711.2) * mm, "end": v(-3526.19, 101.6) * mm});
            skLineSegment(sketch, "E77.right", {"start": v(-3170.59, 711.2) * mm, "end": v(-3170.59, 101.6) * mm});
            skPoint(sketch, "E77.middle", {"position": v(-3348.39, 406.4) * mm});
            skLineSegment(sketch, "E78.bottom", {"start": v(-2103.79, 711.2) * mm, "end": v(-1748.19, 711.2) * mm});
            skLineSegment(sketch, "E78.top", {"start": v(-2103.79, 101.6) * mm, "end": v(-1748.19, 101.6) * mm});
            skLineSegment(sketch, "E78.left", {"start": v(-2103.79, 711.2) * mm, "end": v(-2103.79, 101.6) * mm});
            skLineSegment(sketch, "E78.right", {"start": v(-1748.19, 711.2) * mm, "end": v(-1748.19, 101.6) * mm});
            skPoint(sketch, "E78.middle", {"position": v(-1925.99, 406.4) * mm});
            skLineSegment(sketch, "E79.bottom", {"start": v(-3526.19, -50.8) * mm, "end": v(-3170.59, -50.8) * mm});
            skLineSegment(sketch, "E79.top", {"start": v(-3526.19, -660.4) * mm, "end": v(-3170.59, -660.4) * mm});
            skLineSegment(sketch, "E79.left", {"start": v(-3526.19, -50.8) * mm, "end": v(-3526.19, -660.4) * mm});
            skLineSegment(sketch, "E79.right", {"start": v(-3170.59, -50.8) * mm, "end": v(-3170.59, -660.4) * mm});
            skPoint(sketch, "E79.middle", {"position": v(-3348.39, -355.6) * mm});
            skLineSegment(sketch, "E80.bottom", {"start": v(-2103.79, -50.8) * mm, "end": v(-1748.19, -50.8) * mm});
            skLineSegment(sketch, "E80.top", {"start": v(-2103.79, -660.4) * mm, "end": v(-1748.19, -660.4) * mm});
            skLineSegment(sketch, "E80.left", {"start": v(-2103.79, -50.8) * mm, "end": v(-2103.79, -660.4) * mm});
            skLineSegment(sketch, "E80.right", {"start": v(-1748.19, -50.8) * mm, "end": v(-1748.19, -660.4) * mm});
            skPoint(sketch, "E80.middle", {"position": v(-1925.99, -355.6) * mm});
            skLineSegment(sketch, "E81.bottom", {"start": v(-3526.19, -812.8) * mm, "end": v(-3170.59, -812.8) * mm});
            skLineSegment(sketch, "E81.top", {"start": v(-3526.19, -1422.4) * mm, "end": v(-3170.59, -1422.4) * mm});
            skLineSegment(sketch, "E81.left", {"start": v(-3526.19, -812.8) * mm, "end": v(-3526.19, -1422.4) * mm});
            skLineSegment(sketch, "E81.right", {"start": v(-3170.59, -812.8) * mm, "end": v(-3170.59, -1422.4) * mm});
            skPoint(sketch, "E81.middle", {"position": v(-3348.39, -1117.6) * mm});
            skLineSegment(sketch, "E82.bottom", {"start": v(-2103.79, -812.8) * mm, "end": v(-1748.19, -812.8) * mm});
            skLineSegment(sketch, "E82.top", {"start": v(-2103.79, -1422.4) * mm, "end": v(-1748.19, -1422.4) * mm});
            skLineSegment(sketch, "E82.left", {"start": v(-2103.79, -812.8) * mm, "end": v(-2103.79, -1422.4) * mm});
            skLineSegment(sketch, "E82.right", {"start": v(-1748.19, -812.8) * mm, "end": v(-1748.19, -1422.4) * mm});
            skPoint(sketch, "E82.middle", {"position": v(-1925.99, -1117.6) * mm});
            skLineSegment(sketch, "E83.bottom", {"start": v(-3526.19, -1574.8) * mm, "end": v(-3170.59, -1574.8) * mm});
            skLineSegment(sketch, "E83.top", {"start": v(-3526.19, -2184.4) * mm, "end": v(-3170.59, -2184.4) * mm});
            skLineSegment(sketch, "E83.left", {"start": v(-3526.19, -1574.8) * mm, "end": v(-3526.19, -2184.4) * mm});
            skLineSegment(sketch, "E83.right", {"start": v(-3170.59, -1574.8) * mm, "end": v(-3170.59, -2184.4) * mm});
            skPoint(sketch, "E83.middle", {"position": v(-3348.39, -1879.6) * mm});
            skLineSegment(sketch, "E84.bottom", {"start": v(-2103.79, -1574.8) * mm, "end": v(-1748.19, -1574.8) * mm});
            skLineSegment(sketch, "E84.top", {"start": v(-2103.79, -2184.4) * mm, "end": v(-1748.19, -2184.4) * mm});
            skLineSegment(sketch, "E84.left", {"start": v(-2103.79, -1574.8) * mm, "end": v(-2103.79, -2184.4) * mm});
            skLineSegment(sketch, "E84.right", {"start": v(-1748.19, -1574.8) * mm, "end": v(-1748.19, -2184.4) * mm});
            skPoint(sketch, "E84.middle", {"position": v(-1925.99, -1879.6) * mm});
            skLineSegment(sketch, "E85.bottom", {"start": v(-3526.19, -2336.8) * mm, "end": v(-3170.59, -2336.8) * mm});
            skLineSegment(sketch, "E85.top", {"start": v(-3526.19, -2946.4) * mm, "end": v(-3170.59, -2946.4) * mm});
            skLineSegment(sketch, "E85.left", {"start": v(-3526.19, -2336.8) * mm, "end": v(-3526.19, -2946.4) * mm});
            skLineSegment(sketch, "E85.right", {"start": v(-3170.59, -2336.8) * mm, "end": v(-3170.59, -2946.4) * mm});
            skPoint(sketch, "E85.middle", {"position": v(-3348.39, -2641.6) * mm});
            skLineSegment(sketch, "E86.bottom", {"start": v(-2103.79, -2336.8) * mm, "end": v(-1748.19, -2336.8) * mm});
            skLineSegment(sketch, "E86.top", {"start": v(-2103.79, -2946.4) * mm, "end": v(-1748.19, -2946.4) * mm});
            skLineSegment(sketch, "E86.left", {"start": v(-2103.79, -2336.8) * mm, "end": v(-2103.79, -2946.4) * mm});
            skLineSegment(sketch, "E86.right", {"start": v(-1748.19, -2336.8) * mm, "end": v(-1748.19, -2946.4) * mm});
            skPoint(sketch, "E86.middle", {"position": v(-1925.99, -2641.6) * mm});
            skLineSegment(sketch, "E87.bottom", {"start": v(-3526.19, -3098.8) * mm, "end": v(-3170.59, -3098.8) * mm});
            skLineSegment(sketch, "E87.top", {"start": v(-3526.19, -3708.4) * mm, "end": v(-3170.59, -3708.4) * mm});
            skLineSegment(sketch, "E87.left", {"start": v(-3526.19, -3098.8) * mm, "end": v(-3526.19, -3708.4) * mm});
            skLineSegment(sketch, "E87.right", {"start": v(-3170.59, -3098.8) * mm, "end": v(-3170.59, -3708.4) * mm});
            skPoint(sketch, "E87.middle", {"position": v(-3348.39, -3403.6) * mm});
            skLineSegment(sketch, "E88.bottom", {"start": v(-1748.19, -3098.8) * mm, "end": v(-2103.79, -3098.8) * mm});
            skLineSegment(sketch, "E88.top", {"start": v(-1748.19, -3708.4) * mm, "end": v(-2103.79, -3708.4) * mm});
            skLineSegment(sketch, "E88.left", {"start": v(-1748.19, -3098.8) * mm, "end": v(-1748.19, -3708.4) * mm});
            skLineSegment(sketch, "E88.right", {"start": v(-2103.79, -3098.8) * mm, "end": v(-2103.79, -3708.4) * mm});
            skPoint(sketch, "E88.middle", {"position": v(-1925.99, -3403.6) * mm});
            skSolve(sketch);
        }
        {
            var Q0;
            Q0=makeQuery(id+"F0.imprint","IMPRINT",FACE,{"disambiguationData":[TD([[makeQuery(id+"F0.imprint","IMPRINT",EDGE,{"derivedFrom":sQuery(id+"F0.wireOp",EDGE,"E0")}),-1.0]])]});
            var sketch = newSketch(context, id + "F11", { "sketchPlane" : qUnion([Q0])});
            skLineSegment(sketch, "E89.bottom", {"start": v(-5100.99, 2235.2) * mm, "end": v(-4745.39, 2235.2) * mm});
            skLineSegment(sketch, "E89.top", {"start": v(-5100.99, 1625.6) * mm, "end": v(-4745.39, 1625.6) * mm});
            skLineSegment(sketch, "E89.left", {"start": v(-5100.99, 2235.2) * mm, "end": v(-5100.99, 1625.6) * mm});
            skLineSegment(sketch, "E89.right", {"start": v(-4745.39, 2235.2) * mm, "end": v(-4745.39, 1625.6) * mm});
            skPoint(sketch, "E89.middle", {"position": v(-4923.19, 1930.4) * mm});
            skLineSegment(sketch, "E90.bottom", {"start": v(-5100.99, 1473.2) * mm, "end": v(-4745.39, 1473.2) * mm});
            skLineSegment(sketch, "E90.top", {"start": v(-5100.99, 863.6) * mm, "end": v(-4745.39, 863.6) * mm});
            skLineSegment(sketch, "E90.left", {"start": v(-5100.99, 1473.2) * mm, "end": v(-5100.99, 863.6) * mm});
            skLineSegment(sketch, "E90.right", {"start": v(-4745.39, 1473.2) * mm, "end": v(-4745.39, 863.6) * mm});
            skPoint(sketch, "E90.middle", {"position": v(-4923.19, 1168.4) * mm});
            skLineSegment(sketch, "E91.bottom", {"start": v(-6523.39, 2235.2) * mm, "end": v(-6167.79, 2235.2) * mm});
            skLineSegment(sketch, "E91.top", {"start": v(-6523.39, 1625.6) * mm, "end": v(-6167.79, 1625.6) * mm});
            skLineSegment(sketch, "E91.left", {"start": v(-6523.39, 2235.2) * mm, "end": v(-6523.39, 1625.6) * mm});
            skLineSegment(sketch, "E91.right", {"start": v(-6167.79, 2235.2) * mm, "end": v(-6167.79, 1625.6) * mm});
            skPoint(sketch, "E91.middle", {"position": v(-6345.59, 1930.4) * mm});
            skLineSegment(sketch, "E92.bottom", {"start": v(-6523.39, 1473.2) * mm, "end": v(-6167.79, 1473.2) * mm});
            skLineSegment(sketch, "E92.top", {"start": v(-6523.39, 863.6) * mm, "end": v(-6167.79, 863.6) * mm});
            skLineSegment(sketch, "E92.left", {"start": v(-6523.39, 1473.2) * mm, "end": v(-6523.39, 863.6) * mm});
            skLineSegment(sketch, "E92.right", {"start": v(-6167.79, 1473.2) * mm, "end": v(-6167.79, 863.6) * mm});
            skPoint(sketch, "E92.middle", {"position": v(-6345.59, 1168.4) * mm});
            skLineSegment(sketch, "E93.bottom", {"start": v(-6523.39, 711.2) * mm, "end": v(-6167.79, 711.2) * mm});
            skLineSegment(sketch, "E93.top", {"start": v(-6523.39, 101.6) * mm, "end": v(-6167.79, 101.6) * mm});
            skLineSegment(sketch, "E93.left", {"start": v(-6523.39, 711.2) * mm, "end": v(-6523.39, 101.6) * mm});
            skLineSegment(sketch, "E93.right", {"start": v(-6167.79, 711.2) * mm, "end": v(-6167.79, 101.6) * mm});
            skPoint(sketch, "E93.middle", {"position": v(-6345.59, 406.4) * mm});
            skLineSegment(sketch, "E94.bottom", {"start": v(-5100.99, 711.2) * mm, "end": v(-4745.39, 711.2) * mm});
            skLineSegment(sketch, "E94.top", {"start": v(-5100.99, 101.6) * mm, "end": v(-4745.39, 101.6) * mm});
            skLineSegment(sketch, "E94.left", {"start": v(-5100.99, 711.2) * mm, "end": v(-5100.99, 101.6) * mm});
            skLineSegment(sketch, "E94.right", {"start": v(-4745.39, 711.2) * mm, "end": v(-4745.39, 101.6) * mm});
            skPoint(sketch, "E94.middle", {"position": v(-4923.19, 406.4) * mm});
            skLineSegment(sketch, "E95.bottom", {"start": v(-5100.99, -50.8) * mm, "end": v(-4745.39, -50.8) * mm});
            skLineSegment(sketch, "E95.top", {"start": v(-5100.99, -660.4) * mm, "end": v(-4745.39, -660.4) * mm});
            skLineSegment(sketch, "E95.left", {"start": v(-5100.99, -50.8) * mm, "end": v(-5100.99, -660.4) * mm});
            skLineSegment(sketch, "E95.right", {"start": v(-4745.39, -50.8) * mm, "end": v(-4745.39, -660.4) * mm});
            skPoint(sketch, "E95.middle", {"position": v(-4923.19, -355.6) * mm});
            skLineSegment(sketch, "E96.bottom", {"start": v(-5100.99, -812.8) * mm, "end": v(-4745.39, -812.8) * mm});
            skLineSegment(sketch, "E96.top", {"start": v(-5100.99, -1422.4) * mm, "end": v(-4745.39, -1422.4) * mm});
            skLineSegment(sketch, "E96.left", {"start": v(-5100.99, -812.8) * mm, "end": v(-5100.99, -1422.4) * mm});
            skLineSegment(sketch, "E96.right", {"start": v(-4745.39, -812.8) * mm, "end": v(-4745.39, -1422.4) * mm});
            skPoint(sketch, "E96.middle", {"position": v(-4923.19, -1117.6) * mm});
            skLineSegment(sketch, "E97.bottom", {"start": v(-5100.99, -1574.8) * mm, "end": v(-4745.39, -1574.8) * mm});
            skLineSegment(sketch, "E97.top", {"start": v(-5100.99, -2184.4) * mm, "end": v(-4745.39, -2184.4) * mm});
            skLineSegment(sketch, "E97.left", {"start": v(-5100.99, -1574.8) * mm, "end": v(-5100.99, -2184.4) * mm});
            skLineSegment(sketch, "E97.right", {"start": v(-4745.39, -1574.8) * mm, "end": v(-4745.39, -2184.4) * mm});
            skPoint(sketch, "E97.middle", {"position": v(-4923.19, -1879.6) * mm});
            skLineSegment(sketch, "E98.bottom", {"start": v(-5100.99, -2336.8) * mm, "end": v(-4745.39, -2336.8) * mm});
            skLineSegment(sketch, "E98.top", {"start": v(-5100.99, -2946.4) * mm, "end": v(-4745.39, -2946.4) * mm});
            skLineSegment(sketch, "E98.left", {"start": v(-5100.99, -2336.8) * mm, "end": v(-5100.99, -2946.4) * mm});
            skLineSegment(sketch, "E98.right", {"start": v(-4745.39, -2336.8) * mm, "end": v(-4745.39, -2946.4) * mm});
            skPoint(sketch, "E98.middle", {"position": v(-4923.19, -2641.6) * mm});
            skLineSegment(sketch, "E99.bottom", {"start": v(-4745.39, -3098.8) * mm, "end": v(-5100.99, -3098.8) * mm});
            skLineSegment(sketch, "E99.top", {"start": v(-4745.39, -3708.4) * mm, "end": v(-5100.99, -3708.4) * mm});
            skLineSegment(sketch, "E99.left", {"start": v(-4745.39, -3098.8) * mm, "end": v(-4745.39, -3708.4) * mm});
            skLineSegment(sketch, "E99.right", {"start": v(-5100.99, -3098.8) * mm, "end": v(-5100.99, -3708.4) * mm});
            skPoint(sketch, "E99.middle", {"position": v(-4923.19, -3403.6) * mm});
            skLineSegment(sketch, "E100.bottom", {"start": v(-6167.79, -660.4) * mm, "end": v(-6523.39, -660.4) * mm});
            skLineSegment(sketch, "E100.top", {"start": v(-6167.79, -50.8) * mm, "end": v(-6523.39, -50.8) * mm});
            skLineSegment(sketch, "E100.left", {"start": v(-6167.79, -660.4) * mm, "end": v(-6167.79, -50.8) * mm});
            skLineSegment(sketch, "E100.right", {"start": v(-6523.39, -660.4) * mm, "end": v(-6523.39, -50.8) * mm});
            skLineSegment(sketch, "E101.bottom", {"start": v(-6167.79, -1422.4) * mm, "end": v(-6523.39, -1422.4) * mm});
            skLineSegment(sketch, "E101.top", {"start": v(-6167.79, -812.8) * mm, "end": v(-6523.39, -812.8) * mm});
            skLineSegment(sketch, "E101.left", {"start": v(-6167.79, -1422.4) * mm, "end": v(-6167.79, -812.8) * mm});
            skLineSegment(sketch, "E101.right", {"start": v(-6523.39, -1422.4) * mm, "end": v(-6523.39, -812.8) * mm});
            skLineSegment(sketch, "E102.bottom", {"start": v(-6167.79, -2184.4) * mm, "end": v(-6523.39, -2184.4) * mm});
            skLineSegment(sketch, "E102.top", {"start": v(-6167.79, -1574.8) * mm, "end": v(-6523.39, -1574.8) * mm});
            skLineSegment(sketch, "E102.left", {"start": v(-6167.79, -2184.4) * mm, "end": v(-6167.79, -1574.8) * mm});
            skLineSegment(sketch, "E102.right", {"start": v(-6523.39, -2184.4) * mm, "end": v(-6523.39, -1574.8) * mm});
            skLineSegment(sketch, "E103.bottom", {"start": v(-6167.79, -2946.4) * mm, "end": v(-6523.39, -2946.4) * mm});
            skLineSegment(sketch, "E103.top", {"start": v(-6167.79, -2336.8) * mm, "end": v(-6523.39, -2336.8) * mm});
            skLineSegment(sketch, "E103.left", {"start": v(-6167.79, -2946.4) * mm, "end": v(-6167.79, -2336.8) * mm});
            skLineSegment(sketch, "E103.right", {"start": v(-6523.39, -2946.4) * mm, "end": v(-6523.39, -2336.8) * mm});
            skLineSegment(sketch, "E104.bottom", {"start": v(-6167.79, -3708.4) * mm, "end": v(-6523.39, -3708.4) * mm});
            skLineSegment(sketch, "E104.top", {"start": v(-6167.79, -3098.8) * mm, "end": v(-6523.39, -3098.8) * mm});
            skLineSegment(sketch, "E104.left", {"start": v(-6167.79, -3708.4) * mm, "end": v(-6167.79, -3098.8) * mm});
            skLineSegment(sketch, "E104.right", {"start": v(-6523.39, -3708.4) * mm, "end": v(-6523.39, -3098.8) * mm});
            skSolve(sketch);
        }
        {
            var Q0;
            Q0 = qSketchRegion(id + "F1", true);
            extrude(context, id + "F12", {"entities" : qUnion([Q0]), "depth" : 5486.4 * mm, "offsetDistance" : 25.4 * mm});
        }
        {
            var Q0;
            Q0 = qSketchRegion(id + "F7", true);
            extrude(context, id + "F13", {"entities" : qUnion([Q0]), "depth" : 2133.6 * mm, "offsetDistance" : 25.4 * mm});
        }
        {
            var Q0;
            Q0 = qSketchRegion(id + "F8", true);
            extrude(context, id + "F14", {"entities" : qUnion([Q0]), "depth" : 2133.6 * mm, "offsetDistance" : 25.4 * mm});
        }
        {
            var Q0;
            Q0 = qSketchRegion(id + "F9", true);
            extrude(context, id + "F15", {"entities" : qUnion([Q0]), "depth" : 2133.6 * mm, "offsetDistance" : 25.4 * mm});
        }
        {
            var Q0;
            Q0 = qSketchRegion(id + "F10", true);
            extrude(context, id + "F16", {"entities" : qUnion([Q0]), "depth" : 2133.6 * mm, "offsetDistance" : 25.4 * mm});
        }
        {
            var Q0;
            Q0 = qSketchRegion(id + "F11", true);
            extrude(context, id + "F17", {"entities" : qUnion([Q0]), "depth" : 2133.6 * mm, "offsetDistance" : 25.4 * mm});
        }
        {
            var Q0;
            Q0 = qSketchRegion(id + "F6", true);
            extrude(context, id + "F18", {"entities" : qUnion([Q0]), "depth" : 3657.6 * mm, "offsetDistance" : 25.4 * mm});
        }
        {
            var Q0;
            Q0 = qSketchRegion(id + "F5", true);
            extrude(context, id + "F19", {"entities" : qUnion([Q0]), "depth" : 4267.2 * mm, "offsetDistance" : 25.4 * mm});
        }
        {
            var Q0;
            Q0 = qSketchRegion(id + "F4", true);
            extrude(context, id + "F20", {"entities" : qUnion([Q0]), "depth" : 2743.2 * mm, "offsetDistance" : 25.4 * mm});
        }
        {
            var Q0;
            Q0 = qSketchRegion(id + "F3", true);
            extrude(context, id + "F21", {"entities" : qUnion([Q0]), "depth" : 1016 * mm, "offsetDistance" : 25.4 * mm});
        }
        {
            var Q0;
            Q0 = qSketchRegion(id + "F2", true);
            extrude(context, id + "F22", {"entities" : qUnion([Q0]), "depth" : 2133.6 * mm, "offsetDistance" : 25.4 * mm});
        }
        {
            var Q0;
            Q0 = qSketchRegion(id + "F0", true);
            var Q1;
            Q1=sQuery(id+"F0.wireOp",EDGE,"E0");
            var Q2;
            Q2=sQuery(id+"F0.wireOp",EDGE,"E6");
            var Q3;
            Q3=sQuery(id+"F0.wireOp",EDGE,"E7");
            var Q4;
            Q4=sQuery(id+"F0.wireOp",EDGE,"E8");
            var Q5;
            Q5=sQuery(id+"F0.wireOp",EDGE,"E9");
            var Q6;
            Q6=sQuery(id+"F0.wireOp",EDGE,"E5");
            var Q7;
            Q7=sQuery(id+"F0.wireOp",EDGE,"E4");
            var Q8;
            Q8=sQuery(id+"F0.wireOp",EDGE,"E3");
            var Q9;
            Q9=sQuery(id+"F0.wireOp",EDGE,"E1");
            var Q10;
            Q10=sQuery(id+"F0.wireOp",EDGE,"E2");
            extrude(context, id + "F23", {"entities" : qUnion([Q0]), "bodyType" : ToolBodyType.SURFACE, "surfaceEntities" : qUnion([Q1, Q2, Q3, Q4, Q5, Q6, Q7, Q8, Q9, Q10]), "depth" : 5486.4 * mm, "offsetDistance" : 25.4 * mm});
        }
        {
            var Q0;
            Q0=makeQuery(id+"F0.imprint","IMPRINT",FACE,{"disambiguationData":[TD([[makeQuery(id+"F0.imprint","IMPRINT",EDGE,{"derivedFrom":sQuery(id+"F0.wireOp",EDGE,"E0")}),-1.0]])]});
            var sketch = newSketch(context, id + "F24", { "sketchPlane" : qUnion([Q0])});
            skLineSegment(sketch, "E105.bottom", {"start": v(-9574.21, 1244.6) * mm, "end": v(-10501.31, 1244.6) * mm});
            skLineSegment(sketch, "E105.top", {"start": v(-9574.21, 12.7) * mm, "end": v(-10501.31, 12.7) * mm});
            skLineSegment(sketch, "E105.left", {"start": v(-9574.21, 1244.6) * mm, "end": v(-9574.21, 12.7) * mm});
            skLineSegment(sketch, "E105.right", {"start": v(-10501.31, 1244.6) * mm, "end": v(-10501.31, 12.7) * mm});
            skLineSegment(sketch, "E106.bottom", {"start": v(-10501.31, 2476.5) * mm, "end": v(-9574.21, 2476.5) * mm});
            skLineSegment(sketch, "E106.top", {"start": v(-10501.31, 1244.6) * mm, "end": v(-9574.21, 1244.6) * mm});
            skLineSegment(sketch, "E106.left", {"start": v(-10501.31, 2476.5) * mm, "end": v(-10501.31, 1244.6) * mm});
            skLineSegment(sketch, "E106.right", {"start": v(-9574.21, 2476.5) * mm, "end": v(-9574.21, 1244.6) * mm});
            skCircle(sketch, "E107", {"center": v(-6307.49, 1603.38) * mm, "radius": 38.1 * mm});
            skCircle(sketch, "E108", {"center": v(-6307.49, -225.42) * mm, "radius": 38.1 * mm});
            skCircle(sketch, "E109", {"center": v(-4173.89, 1603.38) * mm, "radius": 38.1 * mm});
            skCircle(sketch, "E110", {"center": v(-4173.89, -225.42) * mm, "radius": 38.1 * mm});
            skCircle(sketch, "E111", {"center": v(-2040.29, -225.42) * mm, "radius": 38.1 * mm});
            skCircle(sketch, "E112", {"center": v(-2040.29, 1603.38) * mm, "radius": 38.1 * mm});
            skCircle(sketch, "E113", {"center": v(93.31, 1603.38) * mm, "radius": 38.1 * mm});
            skCircle(sketch, "E114", {"center": v(93.31, -225.42) * mm, "radius": 38.1 * mm});
            skCircle(sketch, "E115", {"center": v(2226.91, 1603.38) * mm, "radius": 38.1 * mm});
            skCircle(sketch, "E116", {"center": v(2226.91, -225.42) * mm, "radius": 38.1 * mm});
            skCircle(sketch, "E117", {"center": v(5681.31, 612.14) * mm, "radius": 38.1 * mm});
            skCircle(sketch, "E118", {"center": v(4360.51, 1574.8) * mm, "radius": 38.1 * mm});
            skCircle(sketch, "E119", {"center": v(8246.71, 612.14) * mm, "radius": 38.1 * mm});
            skCircle(sketch, "E120", {"center": v(4360.51, -749.3) * mm, "radius": 38.1 * mm});
            skCircle(sketch, "E121", {"center": v(5681.31, -1673.86) * mm, "radius": 38.1 * mm});
            skCircle(sketch, "E122", {"center": v(8246.71, -1673.86) * mm, "radius": 38.1 * mm});
            skCircle(sketch, "E123", {"center": v(8246.71, -3502.66) * mm, "radius": 38.1 * mm});
            skCircle(sketch, "E124", {"center": v(5681.31, -3502.66) * mm, "radius": 38.1 * mm});
            skCircle(sketch, "E125", {"center": v(4360.51, -2578.1) * mm, "radius": 38.1 * mm});
            skCircle(sketch, "E126", {"center": v(1414.11, -2054.23) * mm, "radius": 38.1 * mm});
            skCircle(sketch, "E127", {"center": v(-719.49, -2054.23) * mm, "radius": 38.1 * mm});
            skCircle(sketch, "E128", {"center": v(-2853.09, -2054.23) * mm, "radius": 38.1 * mm});
            skSolve(sketch);
        }
        {
            var Q0;
            Q0 = qSketchRegion(id + "F24", true);
            extrude(context, id + "F25", {"entities" : qUnion([Q0]), "depth" : 2133.6 * mm, "offsetDistance" : 25.4 * mm});
        }
    });
